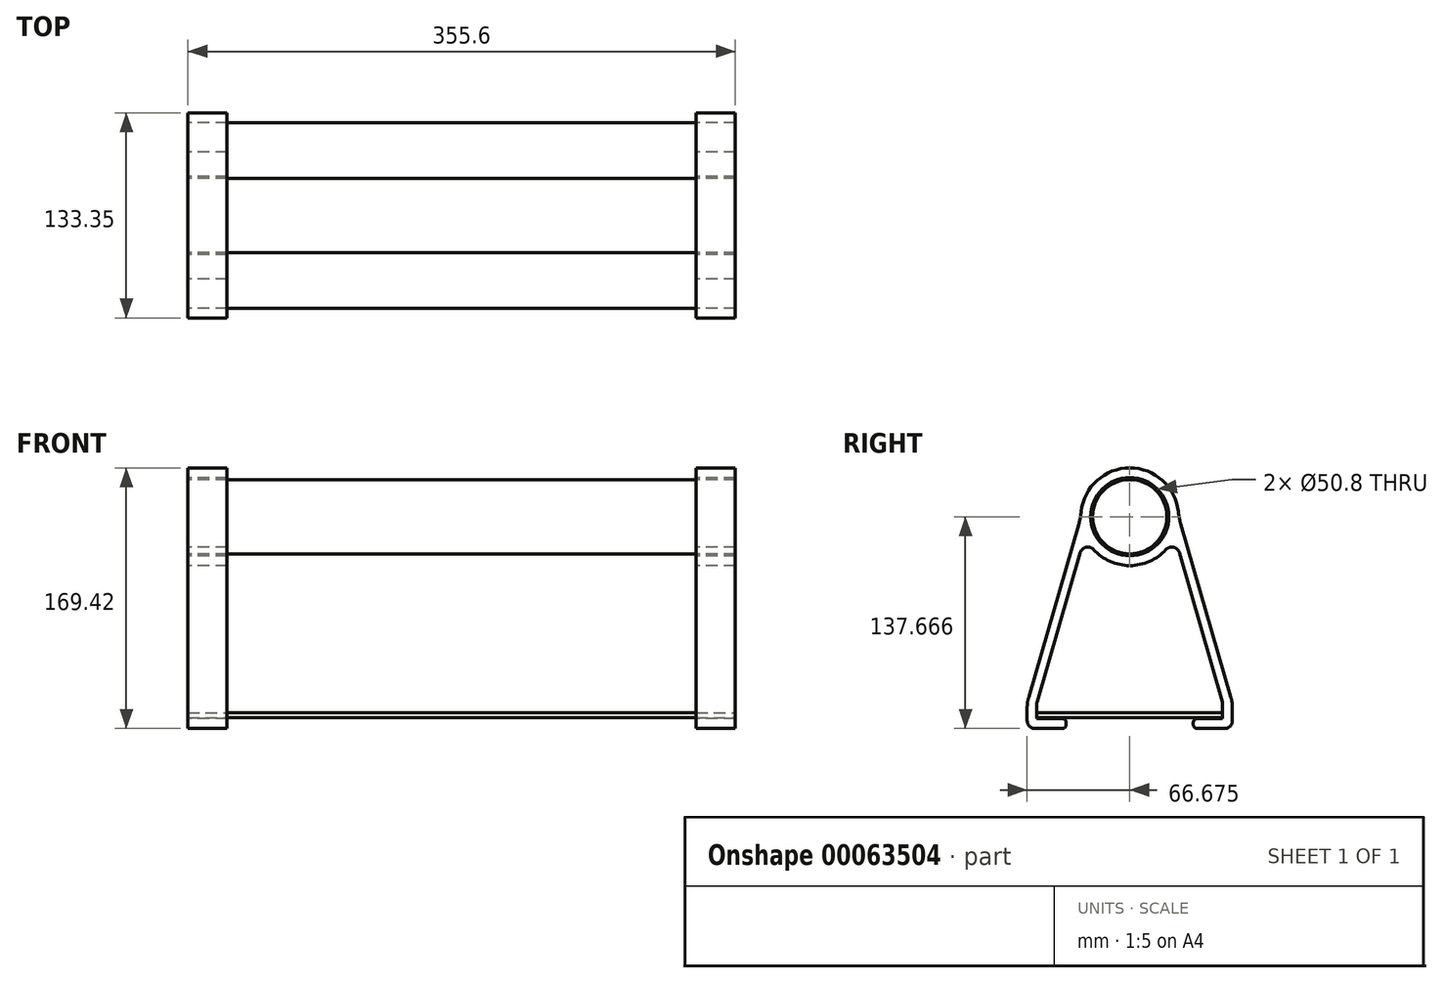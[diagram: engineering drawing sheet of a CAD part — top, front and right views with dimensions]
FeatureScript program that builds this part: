
annotation { "Feature Type Name" : "Feature", "Feature Type Description" : "" }
export const myFeature = defineFeature(function(context is Context, id is Id, definition is map)
    precondition{}
    {
        {
            var Q0;
            Q0=qCreatedBy(makeId("Top.planeOp"),FACE);
            var sketch = newSketch(context, id + "F0", { "sketchPlane" : qUnion([Q0])});
            skLineSegment(sketch, "E0.bottom", {"start": v(0, 0) * mm, "end": v(355.6, 0) * mm});
            skLineSegment(sketch, "E0.top", {"start": v(0, -120.65) * mm, "end": v(355.6, -120.65) * mm});
            skLineSegment(sketch, "E0.left", {"start": v(0, 0) * mm, "end": v(0, -120.65) * mm});
            skLineSegment(sketch, "E0.right", {"start": v(355.6, 0) * mm, "end": v(355.6, -120.65) * mm});
            skSolve(sketch);
        }
        {
            var Q0;
            Q0 = qSketchRegion(id + "F0", true);
            extrude(context, id + "F1", {"entities" : qUnion([Q0]), "depth" : 3.17 * mm});
        }
        {
            var Q0;
            Q0=makeQuery(id+"F1.opExtrude","SWEPT_FACE",FACE,{"disambiguationData":[OSD([sQuery(id+"F0.wireOp",EDGE,"E0.left")])]});
            var sketch = newSketch(context, id + "F2", { "sketchPlane" : qUnion([Q0])});
            skLineSegment(sketch, "E1.rect.bottom", {"start": v(120.65, 3.75) * mm, "end": v(0, 3.75) * mm});
            skLineSegment(sketch, "E1.rect.top", {"start": v(120.65, -0.57) * mm, "end": v(0, -0.57) * mm});
            skLineSegment(sketch, "E1.rect.left", {"start": v(120.65, 3.75) * mm, "end": v(120.65, -0.57) * mm});
            skLineSegment(sketch, "E1.rect.right", {"start": v(0, 3.75) * mm, "end": v(0, -0.57) * mm});
            skPoint(sketch, "E1.rect.middle", {"position": v(60.33, 1.59) * mm});
            skPoint(sketch, "E1.rect.middle.positionSnap0", {"position": v(60.33, 3.18) * mm});
            skPoint(sketch, "E1.rect.middle.positionSnap1", {"position": v(120.65, 1.59) * mm});
            skPoint(sketch, "E1.rect.centerSnap0", {"position": v(60.33, 3.18) * mm});
            skPoint(sketch, "E1.rect.centerSnap1", {"position": v(120.65, 1.59) * mm});
            skLineSegment(sketch, "E2", {"start": v(19.05, 3.75) * mm, "end": v(19.05, -0.57) * mm});
            skLineSegment(sketch, "E3", {"start": v(101.6, 3.75) * mm, "end": v(101.6, -0.57) * mm});
            skLineSegment(sketch, "E4.bottom", {"start": v(0, 3.75) * mm, "end": v(19.05, 3.75) * mm});
            skLineSegment(sketch, "E4.top", {"start": v(0, 10.1) * mm, "end": v(19.05, 10.1) * mm});
            skLineSegment(sketch, "E4.left", {"start": v(0, 3.75) * mm, "end": v(0, 10.1) * mm});
            skLineSegment(sketch, "E4.right", {"start": v(19.05, 3.75) * mm, "end": v(19.05, 10.1) * mm});
            skLineSegment(sketch, "E5.bottom", {"start": v(0, 10.1) * mm, "end": v(-6.35, 10.1) * mm});
            skLineSegment(sketch, "E5.top", {"start": v(0, -0.57) * mm, "end": v(-6.35, -0.57) * mm});
            skLineSegment(sketch, "E5.left", {"start": v(0, 10.1) * mm, "end": v(0, -0.57) * mm});
            skLineSegment(sketch, "E5.right", {"start": v(-6.35, 10.1) * mm, "end": v(-6.35, -0.57) * mm});
            skLineSegment(sketch, "E6.bottom", {"start": v(-6.35, -0.57) * mm, "end": v(19.05, -0.57) * mm});
            skLineSegment(sketch, "E6.top", {"start": v(-6.35, -6.92) * mm, "end": v(19.05, -6.92) * mm});
            skLineSegment(sketch, "E6.left", {"start": v(-6.35, -0.57) * mm, "end": v(-6.35, -6.92) * mm});
            skLineSegment(sketch, "E6.right", {"start": v(19.05, -0.57) * mm, "end": v(19.05, -6.92) * mm});
            skLineSegment(sketch, "E7.bottom", {"start": v(101.6, 3.75) * mm, "end": v(120.65, 3.75) * mm});
            skLineSegment(sketch, "E7.top", {"start": v(101.6, 10.1) * mm, "end": v(120.65, 10.1) * mm});
            skLineSegment(sketch, "E7.left", {"start": v(101.6, 3.75) * mm, "end": v(101.6, 10.1) * mm});
            skLineSegment(sketch, "E7.right", {"start": v(120.65, 3.75) * mm, "end": v(120.65, 10.1) * mm});
            skLineSegment(sketch, "E8.bottom", {"start": v(120.65, 10.1) * mm, "end": v(127, 10.1) * mm});
            skLineSegment(sketch, "E8.top", {"start": v(120.65, -0.57) * mm, "end": v(127, -0.57) * mm});
            skLineSegment(sketch, "E8.left", {"start": v(120.65, 10.1) * mm, "end": v(120.65, -0.57) * mm});
            skLineSegment(sketch, "E8.right", {"start": v(127, 10.1) * mm, "end": v(127, -0.57) * mm});
            skLineSegment(sketch, "E9.bottom", {"start": v(127, -0.57) * mm, "end": v(101.6, -0.57) * mm});
            skLineSegment(sketch, "E9.top", {"start": v(127, -6.92) * mm, "end": v(101.6, -6.92) * mm});
            skLineSegment(sketch, "E9.left", {"start": v(127, -0.57) * mm, "end": v(127, -6.92) * mm});
            skLineSegment(sketch, "E9.right", {"start": v(101.6, -0.57) * mm, "end": v(101.6, -6.92) * mm});
            skLineSegment(sketch, "E10", {"start": v(60.33, 3.75) * mm, "end": v(60.33, 130.75) * mm, "construction": true});
            skPoint(sketch, "E10.endSnap0", {"position": v(60.33, 3.75) * mm});
            skCircle(sketch, "E11", {"center": v(60.33, 130.75) * mm, "radius": 31.75 * mm});
            skCircle(sketch, "E12", {"center": v(60.33, 130.75) * mm, "radius": 25.4 * mm});
            skLineSegment(sketch, "E13", {"start": v(28.58, 130.75) * mm, "end": v(-6.35, 10.1) * mm});
            skLineSegment(sketch, "E14", {"start": v(92.07, 130.75) * mm, "end": v(127, 10.1) * mm});
            skLineSegment(sketch, "E15", {"start": v(0, 10.1) * mm, "end": v(31.24, 118.01) * mm});
            skLineSegment(sketch, "E16", {"start": v(120.65, 10.1) * mm, "end": v(89.41, 118.01) * mm});
            skSolve(sketch);
        }
        {
            var Q0;
            Q0=makeQuery(id+"F2.imprint","IMPRINT",FACE,{"disambiguationData":[TD([[makeQuery(id+"F2.imprint","IMPRINT",EDGE,{"derivedFrom":sQuery(id+"F2.wireOp",EDGE,"E5.bottom")}),-1.0]])]});
            var Q1;
            Q1=makeQuery(id+"F2.imprint","IMPRINT",FACE,{"disambiguationData":[TD([[makeQuery(id+"F2.imprint","IMPRINT",EDGE,{"derivedFrom":sQuery(id+"F2.wireOp",EDGE,"E12")}),-1.0]])]});
            var Q2;
            Q2=makeQuery(id+"F2.imprint","IMPRINT",FACE,{"disambiguationData":[TD([[makeQuery(id+"F2.imprint","IMPRINT",EDGE,{"derivedFrom":sQuery(id+"F2.wireOp",EDGE,"E8.bottom")}),1.0]])]});
            var Q3;
            {var subQ8=sQuery(id+"F2.wireOp",EDGE,"E8.bottom");Q3=makeQuery(id+"F2.imprint","IMPRINT",FACE,{"disambiguationData":[TD([[makeQuery(id+"F2.imprint","IMPRINT",EDGE,{"derivedFrom":subQ8}),-1.0]])]});}
            var Q4;
            {var subQ0=sQuery(id+"F2.wireOp",EDGE,"E7.bottom");Q4=makeQuery(id+"F2.imprint","IMPRINT",FACE,{"disambiguationData":[TD([[makeQuery(id+"F2.imprint","IMPRINT",EDGE,{"derivedFrom":subQ0}),1.0]])]});}
            var Q5;
            Q5=makeQuery(id+"F2.imprint","IMPRINT",FACE,{"disambiguationData":[TD([[makeQuery(id+"F2.imprint","IMPRINT",EDGE,{"derivedFrom":sQuery(id+"F2.wireOp",EDGE,"E9.top")}),-1.0]])]});
            var Q6;
            {var subQ0=sQuery(id+"F2.wireOp",EDGE,"E4.bottom");Q6=makeQuery(id+"F2.imprint","IMPRINT",FACE,{"disambiguationData":[TD([[makeQuery(id+"F2.imprint","IMPRINT",EDGE,{"derivedFrom":subQ0}),1.0]])]});}
            var Q7;
            {var subQ5=sQuery(id+"F2.wireOp",EDGE,"E5.bottom");Q7=makeQuery(id+"F2.imprint","IMPRINT",FACE,{"disambiguationData":[TD([[makeQuery(id+"F2.imprint","IMPRINT",EDGE,{"derivedFrom":subQ5}),1.0]])]});}
            var Q8;
            Q8=makeQuery(id+"F2.imprint","IMPRINT",FACE,{"disambiguationData":[TD([[makeQuery(id+"F2.imprint","IMPRINT",EDGE,{"derivedFrom":sQuery(id+"F2.wireOp",EDGE,"E6.top")}),1.0]])]});
            extrude(context, id + "F3", {"entities" : qUnion([Q0, Q1, Q2, Q3, Q4, Q5, Q6, Q7, Q8]), "oppositeDirection" : true, "depth" : 25.4 * mm});
        }
        {
            var Q0;
            Q0=makeQuery(id+"F3.opExtrude","SWEPT_EDGE",EDGE,{"disambiguationData":[OSD([sQuery(id+"F2.wireOp",EDGE,"E1.rect.bottom"),sQuery(id+"F2.wireOp",EDGE,"E2"),sQuery(id+"F2.wireOp",EDGE,"E4.bottom"),sQuery(id+"F2.wireOp",EDGE,"E4.right")])]});
            var Q1;
            Q1=makeQuery(id+"F3.opExtrude","SWEPT_EDGE",EDGE,{"disambiguationData":[OSD([sQuery(id+"F2.wireOp",EDGE,"E4.top"),sQuery(id+"F2.wireOp",EDGE,"E4.right")])]});
            var Q2;
            Q2=makeQuery(id+"F3.opExtrude","SWEPT_EDGE",EDGE,{"disambiguationData":[OSD([sQuery(id+"F2.wireOp",EDGE,"E1.rect.top"),sQuery(id+"F2.wireOp",EDGE,"E2"),sQuery(id+"F2.wireOp",EDGE,"E6.bottom"),sQuery(id+"F2.wireOp",EDGE,"E6.right")])]});
            var Q3;
            Q3=makeQuery(id+"F3.opExtrude","SWEPT_EDGE",EDGE,{"disambiguationData":[OSD([sQuery(id+"F2.wireOp",EDGE,"E6.top"),sQuery(id+"F2.wireOp",EDGE,"E6.right")])]});
            var Q4;
            Q4=makeQuery(id+"F3.opExtrude","SWEPT_EDGE",EDGE,{"disambiguationData":[OSD([sQuery(id+"F2.wireOp",EDGE,"E7.top"),sQuery(id+"F2.wireOp",EDGE,"E7.left")])]});
            var Q5;
            Q5=makeQuery(id+"F3.opExtrude","SWEPT_EDGE",EDGE,{"disambiguationData":[OSD([sQuery(id+"F2.wireOp",EDGE,"E1.rect.bottom"),sQuery(id+"F2.wireOp",EDGE,"E3"),sQuery(id+"F2.wireOp",EDGE,"E7.bottom"),sQuery(id+"F2.wireOp",EDGE,"E7.left")])]});
            var Q6;
            Q6=makeQuery(id+"F3.opExtrude","SWEPT_EDGE",EDGE,{"disambiguationData":[OSD([sQuery(id+"F2.wireOp",EDGE,"E9.top"),sQuery(id+"F2.wireOp",EDGE,"E9.right")])]});
            var Q7;
            Q7=makeQuery(id+"F3.opExtrude","SWEPT_EDGE",EDGE,{"disambiguationData":[OSD([sQuery(id+"F2.wireOp",EDGE,"E1.rect.top"),sQuery(id+"F2.wireOp",EDGE,"E3"),sQuery(id+"F2.wireOp",EDGE,"E9.bottom"),sQuery(id+"F2.wireOp",EDGE,"E9.right")])]});
            fillet(context, id + "F4", {"entities" : qUnion([Q0, Q1, Q2, Q3, Q4, Q5, Q6, Q7]), "radius" : 2.54 * mm, "tangentPropagation" : true, "allowEdgeOverflow" : false});
        }
        {
            var Q0;
            Q0=makeQuery(id+"F3.opExtrude","SWEPT_EDGE",EDGE,{"disambiguationData":[OSD([sQuery(id+"F2.wireOp",EDGE,"E4.top"),sQuery(id+"F2.wireOp",EDGE,"E5.bottom"),sQuery(id+"F2.wireOp",EDGE,"E5.left"),sQuery(id+"F2.wireOp",EDGE,"E15")])]});
            var Q1;
            Q1=makeQuery(id+"F3.opExtrude","SWEPT_EDGE",EDGE,{"disambiguationData":[OSD([sQuery(id+"F2.wireOp",EDGE,"E7.top"),sQuery(id+"F2.wireOp",EDGE,"E8.bottom"),sQuery(id+"F2.wireOp",EDGE,"E8.left"),sQuery(id+"F2.wireOp",EDGE,"E16")])]});
            var Q2;
            Q2=makeQuery(id+"F3.opExtrude","SWEPT_EDGE",EDGE,{"disambiguationData":[OSD([sQuery(id+"F2.wireOp",EDGE,"E6.top"),sQuery(id+"F2.wireOp",EDGE,"E6.left")])]});
            var Q3;
            Q3=makeQuery(id+"F3.opExtrude","SWEPT_EDGE",EDGE,{"disambiguationData":[OSD([sQuery(id+"F2.wireOp",EDGE,"E9.top"),sQuery(id+"F2.wireOp",EDGE,"E9.left")])]});
            var Q4;
            Q4=makeQuery(id+"F3.opExtrude","SWEPT_EDGE",EDGE,{"disambiguationData":[OSD([sQuery(id+"F2.wireOp",EDGE,"E11"),sQuery(id+"F2.wireOp",EDGE,"E15")])]});
            var Q5;
            Q5=makeQuery(id+"F3.opExtrude","SWEPT_EDGE",EDGE,{"disambiguationData":[OSD([sQuery(id+"F2.wireOp",EDGE,"E11"),sQuery(id+"F2.wireOp",EDGE,"E16")])]});
            fillet(context, id + "F5", {"entities" : qUnion([Q0, Q1, Q2, Q3, Q4, Q5]), "radius" : 5.08 * mm, "tangentPropagation" : true, "allowEdgeOverflow" : false});
        }
        {
            var Q0;
            Q0=makeQuery(id+"F3.opExtrude","SWEPT_EDGE",EDGE,{"disambiguationData":[OSD([sQuery(id+"F2.wireOp",EDGE,"E5.bottom"),sQuery(id+"F2.wireOp",EDGE,"E5.right"),sQuery(id+"F2.wireOp",EDGE,"E13")])]});
            var Q1;
            Q1=makeQuery(id+"F3.opExtrude","SWEPT_EDGE",EDGE,{"disambiguationData":[OSD([sQuery(id+"F2.wireOp",EDGE,"E8.bottom"),sQuery(id+"F2.wireOp",EDGE,"E8.right"),sQuery(id+"F2.wireOp",EDGE,"E14")])]});
            fillet(context, id + "F6", {"entities" : qUnion([Q0, Q1]), "radius" : 25.4 * mm, "tangentPropagation" : true, "allowEdgeOverflow" : false});
        }
        {
            var Q0;
            Q0=makeQuery(id+"F3.opExtrude","SWEPT_EDGE",EDGE,{"disambiguationData":[OSD([sQuery(id+"F2.wireOp",EDGE,"E11"),sQuery(id+"F2.wireOp",EDGE,"E13")])]});
            var Q1;
            Q1=makeQuery(id+"F3.opExtrude","SWEPT_EDGE",EDGE,{"disambiguationData":[OSD([sQuery(id+"F2.wireOp",EDGE,"E11"),sQuery(id+"F2.wireOp",EDGE,"E14")])]});
            fillet(context, id + "F7", {"entities" : qUnion([Q0, Q1]), "radius" : 50.8 * mm, "tangentPropagation" : true, "allowEdgeOverflow" : false});
        }
        {
            var Q0;
            Q0=makeQuery(id+"F3.opExtrude","CAP_FACE",FACE,{"disambiguationData":[OSD([sQuery(id+"F2.wireOp",EDGE,"E4.bottom"),sQuery(id+"F2.wireOp",EDGE,"E4.top"),sQuery(id+"F2.wireOp",EDGE,"E4.right"),sQuery(id+"F2.wireOp",EDGE,"E5.left"),sQuery(id+"F2.wireOp",EDGE,"E5.right"),sQuery(id+"F2.wireOp",EDGE,"E6.bottom"),sQuery(id+"F2.wireOp",EDGE,"E6.top"),sQuery(id+"F2.wireOp",EDGE,"E6.left"),sQuery(id+"F2.wireOp",EDGE,"E6.right"),sQuery(id+"F2.wireOp",EDGE,"E7.bottom"),sQuery(id+"F2.wireOp",EDGE,"E7.top"),sQuery(id+"F2.wireOp",EDGE,"E7.left"),sQuery(id+"F2.wireOp",EDGE,"E8.left"),sQuery(id+"F2.wireOp",EDGE,"E8.right"),sQuery(id+"F2.wireOp",EDGE,"E9.bottom"),sQuery(id+"F2.wireOp",EDGE,"E9.top"),sQuery(id+"F2.wireOp",EDGE,"E9.left"),sQuery(id+"F2.wireOp",EDGE,"E9.right"),sQuery(id+"F2.wireOp",EDGE,"E11"),sQuery(id+"F2.wireOp",EDGE,"E12"),sQuery(id+"F2.wireOp",EDGE,"E13"),sQuery(id+"F2.wireOp",EDGE,"E14"),sQuery(id+"F2.wireOp",EDGE,"E15"),sQuery(id+"F2.wireOp",EDGE,"E16")])],"isStart":true});
            var sketch = newSketch(context, id + "F8", { "sketchPlane" : qUnion([Q0])});
            skCircle(sketch, "E17", {"center": v(60.33, 130.75) * mm, "radius": 24.13 * mm});
            skSolve(sketch);
        }
        {
            var Q0;
            Q0=makeQuery(id+"F8.imprint","IMPRINT",FACE,{"disambiguationData":[TD([[makeQuery(id+"F8.imprint","IMPRINT",EDGE,{"derivedFrom":sQuery(id+"F8.wireOp",EDGE,"E17")}),1.0]])]});
            extrude(context, id + "F9", {"entities" : qUnion([Q0]), "oppositeDirection" : true, "depth" : 355.6 * mm});
        }
        {
            var Q0;
            Q0=makeQuery(id+"F3.opExtrude","SWEPT_BODY",BODY,{"disambiguationData":[OSD([sQuery(id+"F2.wireOp",EDGE,"E4.bottom"),sQuery(id+"F2.wireOp",EDGE,"E4.top"),sQuery(id+"F2.wireOp",EDGE,"E4.right"),sQuery(id+"F2.wireOp",EDGE,"E5.left"),sQuery(id+"F2.wireOp",EDGE,"E5.right"),sQuery(id+"F2.wireOp",EDGE,"E6.bottom"),sQuery(id+"F2.wireOp",EDGE,"E6.top"),sQuery(id+"F2.wireOp",EDGE,"E6.left"),sQuery(id+"F2.wireOp",EDGE,"E6.right"),sQuery(id+"F2.wireOp",EDGE,"E7.bottom"),sQuery(id+"F2.wireOp",EDGE,"E7.top"),sQuery(id+"F2.wireOp",EDGE,"E7.left"),sQuery(id+"F2.wireOp",EDGE,"E8.left"),sQuery(id+"F2.wireOp",EDGE,"E8.right"),sQuery(id+"F2.wireOp",EDGE,"E9.bottom"),sQuery(id+"F2.wireOp",EDGE,"E9.top"),sQuery(id+"F2.wireOp",EDGE,"E9.left"),sQuery(id+"F2.wireOp",EDGE,"E9.right"),sQuery(id+"F2.wireOp",EDGE,"E11"),sQuery(id+"F2.wireOp",EDGE,"E12"),sQuery(id+"F2.wireOp",EDGE,"E13"),sQuery(id+"F2.wireOp",EDGE,"E14"),sQuery(id+"F2.wireOp",EDGE,"E15"),sQuery(id+"F2.wireOp",EDGE,"E16")])]});
            transform(context, id + "F10", {"entities" : qUnion([Q0]), "transformType" : TransformType.TRANSLATION_3D, "dx" : 330.2 * mm, "dy" : 0 * mm, "dz" : 0 * mm, "makeCopy" : true});
        }
    });
